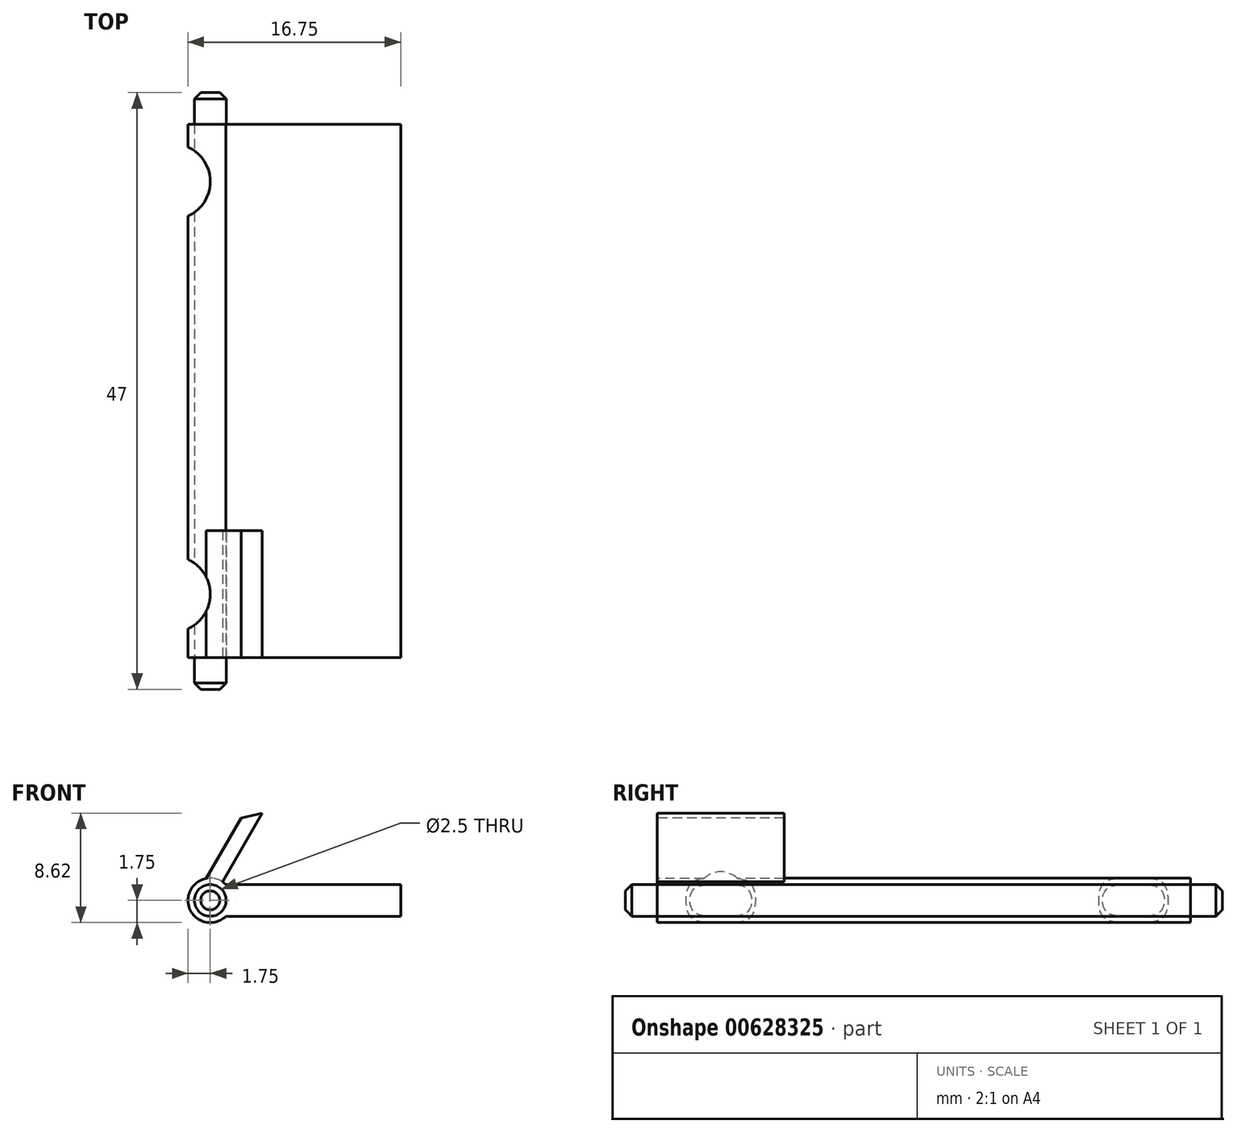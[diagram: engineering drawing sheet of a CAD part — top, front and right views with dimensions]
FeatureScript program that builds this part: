
annotation { "Feature Type Name" : "Feature", "Feature Type Description" : "" }
export const myFeature = defineFeature(function(context is Context, id is Id, definition is map)
    precondition{}
    {
        {
            var Q0;
            Q0=qCreatedBy(makeId("Front.planeOp"),FACE);
            var sketch = newSketch(context, id + "F0", { "sketchPlane" : qUnion([Q0])});
            skCircle(sketch, "E0", {"center": v(0, 0) * mm, "radius": 1.75 * mm});
            skLineSegment(sketch, "E1.bottom", {"start": v(1.22, -1.25) * mm, "end": v(15, -1.25) * mm});
            skLineSegment(sketch, "E1.top", {"start": v(1.22, 1.25) * mm, "end": v(15, 1.25) * mm});
            skLineSegment(sketch, "E1.left", {"start": v(1.22, 1.25) * mm, "end": v(1.22, -1.25) * mm});
            skLineSegment(sketch, "E1.right", {"start": v(15, 1.25) * mm, "end": v(15, -1.25) * mm});
            skLineSegment(sketch, "E2", {"start": v(0.84, 1.25) * mm, "end": v(0.96, 1.46) * mm});
            skLineSegment(sketch, "E3", {"start": v(-0.3, 1.72) * mm, "end": v(2.44, 6.49) * mm});
            skLineSegment(sketch, "E4", {"start": v(4.09, 6.87) * mm, "end": v(2.44, 6.49) * mm});
            skCircle(sketch, "E5", {"center": v(0, 0) * mm, "radius": 1.25 * mm});
            skLineSegment(sketch, "E6.trimOffspring", {"start": v(0.84, 1.25) * mm, "end": v(4.09, 6.87) * mm});
            skSolve(sketch);
        }
        {
            var Q0;
            Q0=makeQuery(id+"F0.imprint","IMPRINT",FACE,{"disambiguationData":[TD([[makeQuery(id+"F0.imprint","IMPRINT",EDGE,{"derivedFrom":sQuery(id+"F0.wireOp",EDGE,"E5")}),1.0]])]});
            extrude(context, id + "F1", {"entities" : qUnion([Q0]), "depth" : 2.5 * mm, "offsetDistance" : 25 * mm});
        }
        {
            var Q0;
            Q0=makeQuery(id+"F1.opExtrude","CAP_EDGE",EDGE,{"disambiguationData":[OSD([sQuery(id+"F0.wireOp",EDGE,"E5")])],"isStart":false});
            chamfer(context, id + "F2", {"entities" : qUnion([Q0]), "width" : 0.5 * mm, "tangentPropagation" : true});
        }
        {
            var Q0;
            {var subQ1=sQuery(id+"F0.wireOp",EDGE,"E1.bottom");Q0=makeQuery(id+"F0.imprint","IMPRINT",FACE,{"disambiguationData":[TD([[makeQuery(id+"F0.imprint","IMPRINT",EDGE,{"derivedFrom":subQ1}),1.0]])]});}
            var Q1;
            {var subQ0=sQuery(id+"F0.wireOp",EDGE,"E1.left");Q1=makeQuery(id+"F0.imprint","IMPRINT",FACE,{"disambiguationData":[TD([[makeQuery(id+"F0.imprint","IMPRINT",EDGE,{"derivedFrom":subQ0}),-1.0]])]});}
            var Q2;
            {var subQ0=sQuery(id+"F0.wireOp",EDGE,"E1.left");Q2=makeQuery(id+"F0.imprint","IMPRINT",FACE,{"disambiguationData":[TD([[makeQuery(id+"F0.imprint","IMPRINT",EDGE,{"derivedFrom":subQ0}),1.0]])]});}
            extrude(context, id + "F3", {"entities" : qUnion([Q0, Q1, Q2]), "operationType" : NewBodyOperationType.ADD, "oppositeDirection" : true, "depth" : 42 * mm, "offsetDistance" : 25 * mm});
        }
        {
            var Q0;
            Q0=makeQuery(id+"F0.imprint","IMPRINT",FACE,{"disambiguationData":[TD([[makeQuery(id+"F0.imprint","IMPRINT",EDGE,{"derivedFrom":sQuery(id+"F0.wireOp",EDGE,"E5")}),1.0]])]});
            extrude(context, id + "F4", {"entities" : qUnion([Q0]), "oppositeDirection" : true, "depth" : 44.5 * mm, "offsetDistance" : 25 * mm});
        }
        {
            var Q0;
            Q0=makeQuery(id+"F4.opExtrude","CAP_EDGE",EDGE,{"disambiguationData":[OSD([sQuery(id+"F0.wireOp",EDGE,"E5")])],"isStart":false});
            chamfer(context, id + "F5", {"entities" : qUnion([Q0]), "width" : 0.5 * mm, "tangentPropagation" : true});
        }
        {
            var Q0;
            Q0=makeQuery(id+"F3.opExtrude","SWEPT_FACE",FACE,{"disambiguationData":[OSD([sQuery(id+"F0.wireOp",EDGE,"E1.top")])]});
            var sketch = newSketch(context, id + "F6", { "sketchPlane" : qUnion([Q0])});
            skCircle(sketch, "E7", {"center": v(-3, 5) * mm, "radius": 3 * mm});
            skCircle(sketch, "E8", {"center": v(-3, 37.5) * mm, "radius": 3 * mm});
            skSolve(sketch);
        }
        {
            var Q0;
            {var subQ0=sQuery(id+"F0.wireOp",EDGE,"E3");Q0=makeQuery(id+"F0.imprint","IMPRINT",FACE,{"disambiguationData":[TD([[makeQuery(id+"F0.imprint","IMPRINT",EDGE,{"derivedFrom":subQ0}),-1.0]])]});}
            extrude(context, id + "F7", {"entities" : qUnion([Q0]), "operationType" : NewBodyOperationType.ADD, "oppositeDirection" : true, "depth" : 10 * mm, "offsetDistance" : 25 * mm});
        }
        {
            var Q0;
            Q0=makeQuery(id+"F6.imprint","IMPRINT",FACE,{"disambiguationData":[TD([[makeQuery(id+"F6.imprint","IMPRINT",EDGE,{"derivedFrom":sQuery(id+"F6.wireOp",EDGE,"E8")}),1.0]])]});
            var Q1;
            Q1=makeQuery(id+"F6.imprint","IMPRINT",FACE,{"disambiguationData":[TD([[makeQuery(id+"F6.imprint","IMPRINT",EDGE,{"derivedFrom":sQuery(id+"F6.wireOp",EDGE,"E7")}),1.0]])]});
            extrude(context, id + "F8", {"entities" : qUnion([Q0, Q1]), "operationType" : NewBodyOperationType.REMOVE, "oppositeDirection" : true, "depth" : 10 * mm, "offsetDistance" : 25 * mm, "hasSecondDirection" : true, "secondDirectionOppositeDirection" : false, "secondDirectionDepth" : 10 * mm});
        }
        {
            var Q0;
            Q0=makeQuery(id+"F3.opExtrude","SWEPT_BODY",BODY,{"disambiguationData":[OSD([sQuery(id+"F0.wireOp",EDGE,"E0"),sQuery(id+"F0.wireOp",EDGE,"E1.bottom"),sQuery(id+"F0.wireOp",EDGE,"E1.top"),sQuery(id+"F0.wireOp",EDGE,"E1.right"),sQuery(id+"F0.wireOp",EDGE,"E5")])]});
            var Q1;
            Q1=makeQuery(id+"F1.opExtrude","SWEPT_BODY",BODY,{"disambiguationData":[OSD([sQuery(id+"F0.wireOp",EDGE,"E5")])]});
            var Q2;
            Q2=makeQuery(id+"F4.opExtrude","SWEPT_BODY",BODY,{"disambiguationData":[OSD([sQuery(id+"F0.wireOp",EDGE,"E5")])]});
            var Q3;
            Q3=makeQuery(id+"F3.opExtrude","SWEPT_FACE",FACE,{"disambiguationData":[OSD([sQuery(id+"F0.wireOp",EDGE,"E1.right")])]});
            mirror(context, id + "F9", {"operationType" : NewBodyOperationType.REMOVE, "entities" : qUnion([Q0, Q1, Q2]), "mirrorPlane" : qUnion([Q3])});
        }
    });
